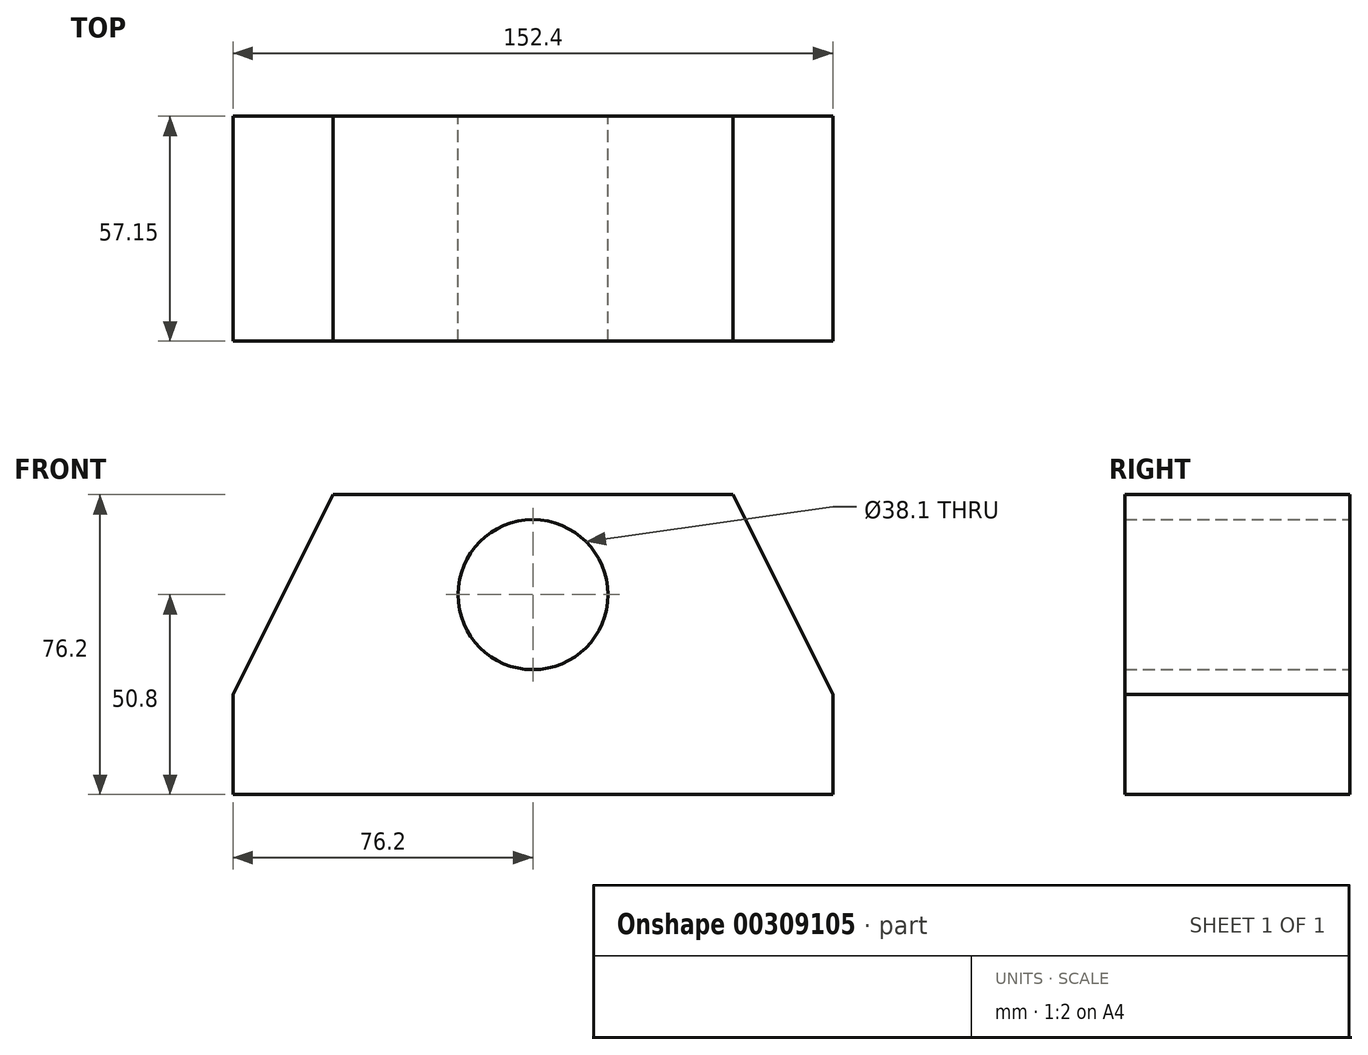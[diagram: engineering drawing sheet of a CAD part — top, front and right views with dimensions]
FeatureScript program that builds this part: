
annotation { "Feature Type Name" : "Feature", "Feature Type Description" : "" }
export const myFeature = defineFeature(function(context is Context, id is Id, definition is map)
    precondition{}
    {
        {
            var Q0;
            Q0=qCreatedBy(makeId("Front.planeOp"),FACE);
            var sketch = newSketch(context, id + "F0", { "sketchPlane" : qUnion([Q0])});
            skLineSegment(sketch, "E0", {"start": v(0, 0) * mm, "end": v(152.4, 0) * mm});
            skLineSegment(sketch, "E1", {"start": v(152.4, 0) * mm, "end": v(152.4, 25.4) * mm});
            skLineSegment(sketch, "E2", {"start": v(0, 25.4) * mm, "end": v(0, 0) * mm});
            skLineSegment(sketch, "E3", {"start": v(0, 25.4) * mm, "end": v(25.4, 76.2) * mm});
            skLineSegment(sketch, "E4", {"start": v(25.4, 76.2) * mm, "end": v(127, 76.2) * mm});
            skLineSegment(sketch, "E5", {"start": v(127, 76.2) * mm, "end": v(152.4, 25.4) * mm});
            skCircle(sketch, "E6", {"center": v(76.2, 50.8) * mm, "radius": 19.05 * mm});
            skSolve(sketch);
        }
        {
            var Q0;
            Q0 = qSketchRegion(id + "F0", true);
            extrude(context, id + "F1", {"entities" : qUnion([Q0]), "depth" : 57.15 * mm});
        }
    });
